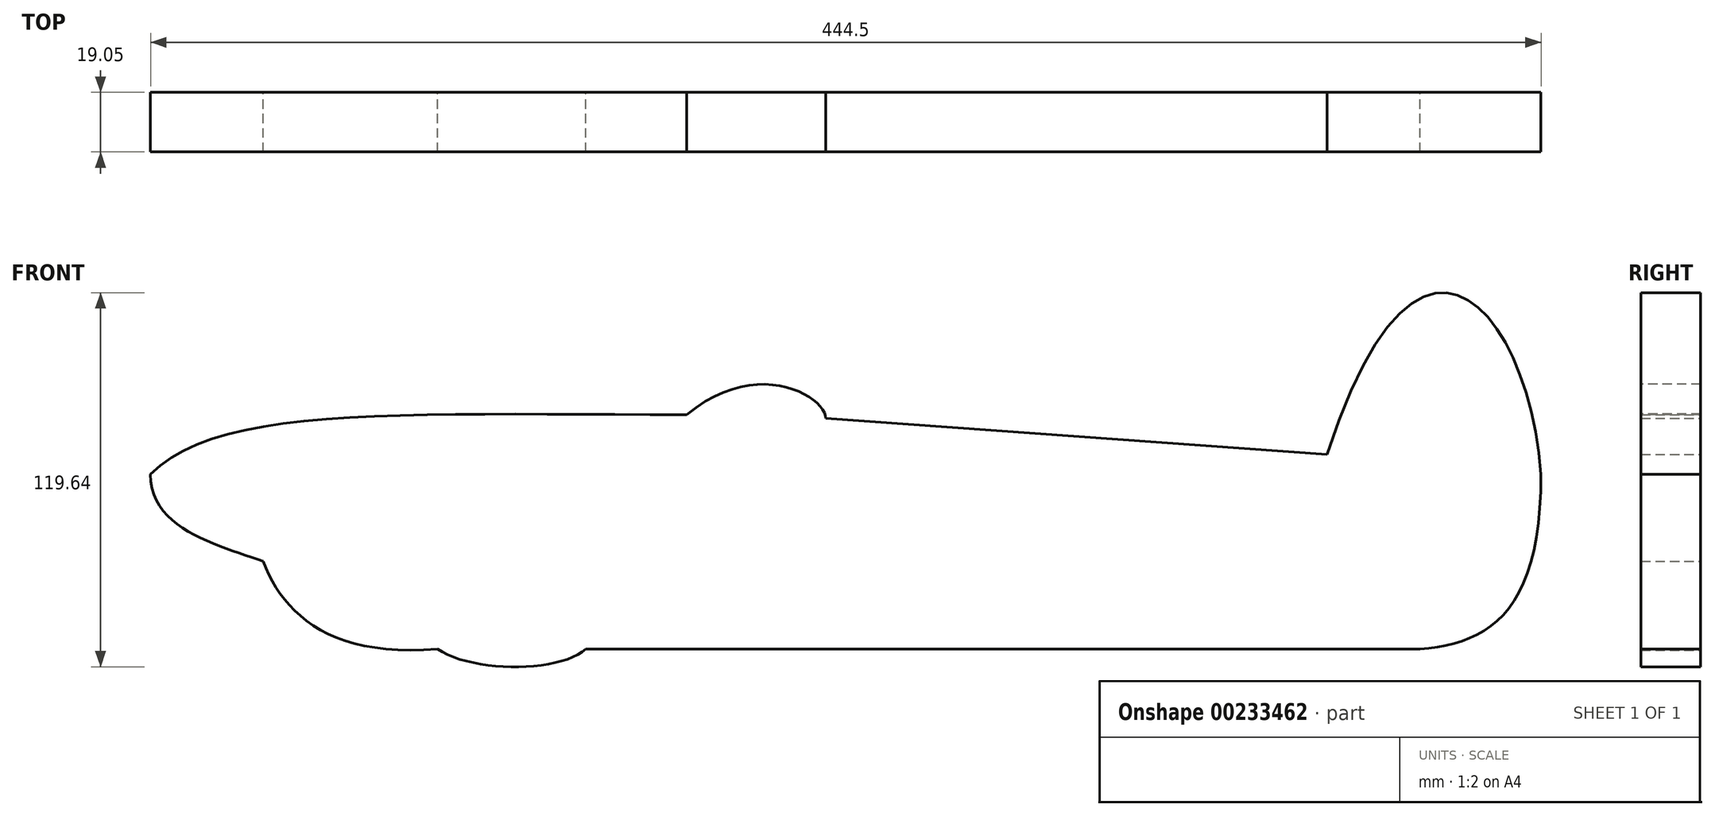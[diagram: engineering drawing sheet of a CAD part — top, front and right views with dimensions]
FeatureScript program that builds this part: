
annotation { "Feature Type Name" : "Feature", "Feature Type Description" : "" }
export const myFeature = defineFeature(function(context is Context, id is Id, definition is map)
    precondition{}
    {
        {
            var Q0;
            Q0=qCreatedBy(makeId("Front.planeOp"),FACE);
            var sketch = newSketch(context, id + "F0", { "sketchPlane" : qUnion([Q0])});
            skPoint(sketch, "E0.middle", {"position": v(130.47, 12.52) * mm});
            skLineSegment(sketch, "E1", {"start": v(314.01, -11.63) * mm, "end": v(47.31, -11.63) * mm});
            skFitSpline(sketch, "E2", {"points": [v(47.31, -11.63) * mm, v(0, -11.63) * mm], "startDerivative": vector(-24.07, -22.78) * mm, "endDerivative": vector(-32.25, 22.78) * mm});
            skFitSpline(sketch, "E3", {"points": [v(-91.78, 44.27) * mm, v(79.67, 63.32) * mm], "startDerivative": vector(66.81, 67.13) * mm, "endDerivative": vector(273.8, 0.17) * mm});
            skLineSegment(sketch, "E4", {"start": v(107, 63.32) * mm, "end": v(284.34, 50.55) * mm});
            skFitSpline(sketch, "E5", {"points": [v(284.34, 50.55) * mm, v(352.72, 44.27) * mm], "startDerivative": vector(86.08, 267.9) * mm, "endDerivative": vector(12.38, -159.28) * mm});
            skFitSpline(sketch, "E6", {"points": [v(352.72, 44.27) * mm, v(314.01, -11.63) * mm], "startDerivative": vector(0, -132.82) * mm, "endDerivative": vector(-65.74, -5.18) * mm});
            skFitSpline(sketch, "E7", {"points": [v(79.67, 63.32) * mm, v(124.12, 62.1) * mm], "startDerivative": vector(68.34, 56.59) * mm, "endDerivative": vector(0, -20.26) * mm});
            skFitSpline(sketch, "E8", {"points": [v(-91.78, 44.27) * mm, v(-55.82, 16.4) * mm], "startDerivative": vector(0, -54.65) * mm, "endDerivative": vector(40.03, -15.18) * mm});
            skFitSpline(sketch, "E9", {"points": [v(-55.82, 16.4) * mm, v(0, -11.63) * mm], "startDerivative": vector(19.32, -49.18) * mm, "endDerivative": vector(105.35, 8.4) * mm});
            skSolve(sketch);
        }
        {
            var Q0;
            Q0 = qSketchRegion(id + "F0", true);
            extrude(context, id + "F1", {"entities" : qUnion([Q0]), "depth" : 19.05 * mm});
        }
    });
